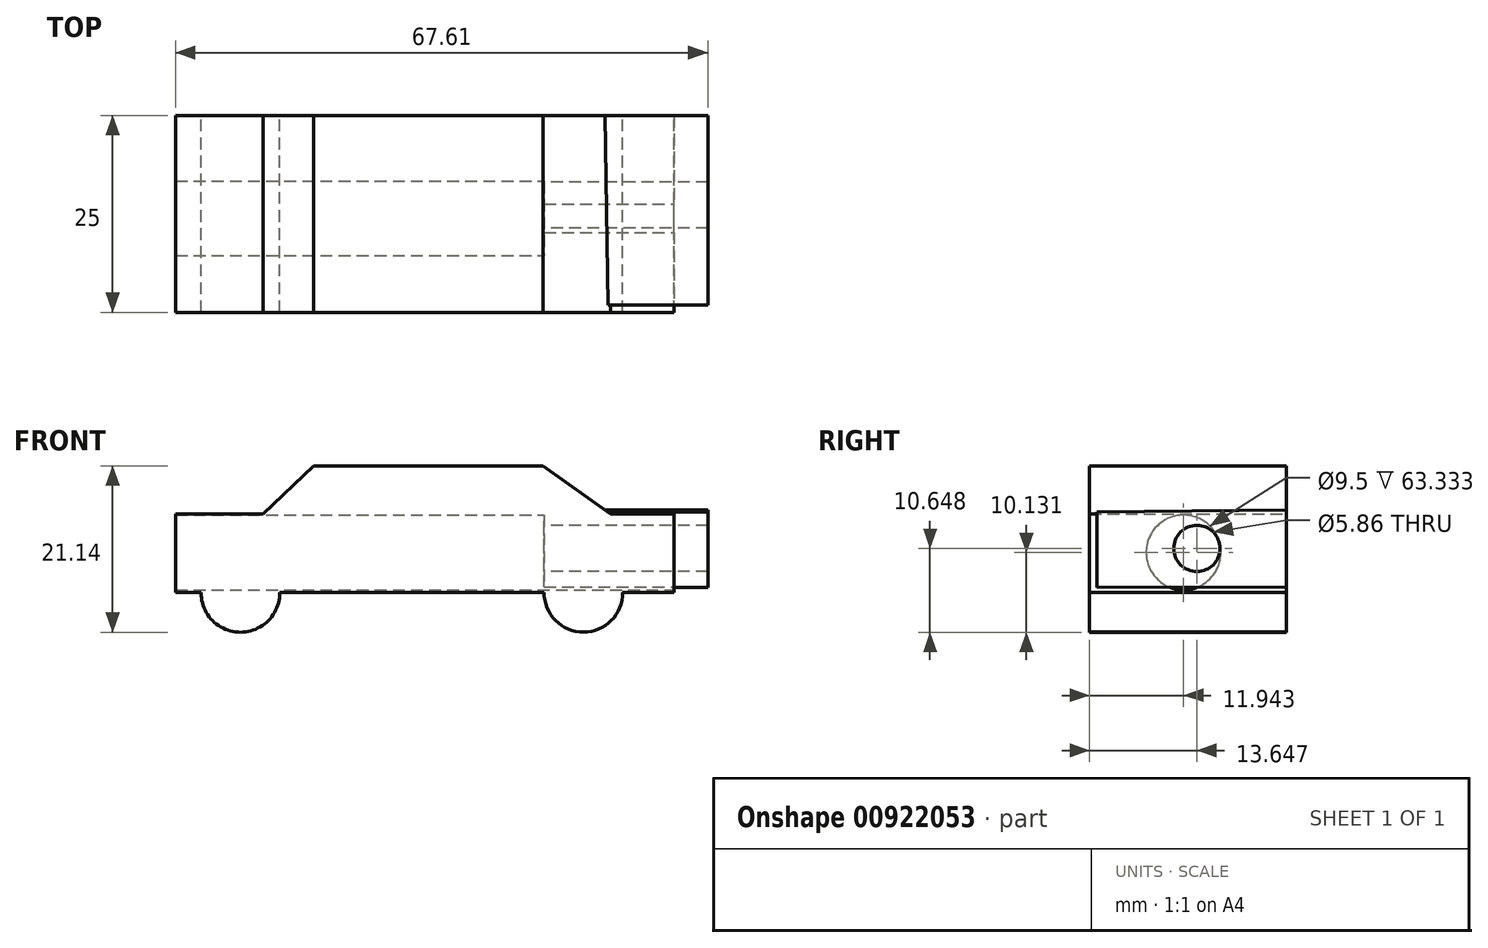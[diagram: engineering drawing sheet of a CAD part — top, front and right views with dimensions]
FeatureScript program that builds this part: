
annotation { "Feature Type Name" : "Feature", "Feature Type Description" : "" }
export const myFeature = defineFeature(function(context is Context, id is Id, definition is map)
    precondition{}
    {
        {
            var Q0;
            Q0=qCreatedBy(makeId("Front.planeOp"),FACE);
            var sketch = newSketch(context, id + "F0", { "sketchPlane" : qUnion([Q0])});
            skLineSegment(sketch, "E0", {"start": v(16.23, 9.06) * mm, "end": v(15.52, 9.06) * mm});
            skLineSegment(sketch, "E1", {"start": v(-46.8, 12.92) * mm, "end": v(-46.8, 22.92) * mm});
            skLineSegment(sketch, "E2", {"start": v(-46.8, 22.92) * mm, "end": v(-35.7, 22.92) * mm});
            skLineSegment(sketch, "E3", {"start": v(-35.7, 22.92) * mm, "end": v(-29.3, 29.03) * mm});
            skLineSegment(sketch, "E4", {"start": v(-29.3, 29.03) * mm, "end": v(0, 29.03) * mm});
            skLineSegment(sketch, "E5", {"start": v(-0.14, 29.03) * mm, "end": v(8.47, 22.92) * mm});
            skLineSegment(sketch, "E6", {"start": v(8.47, 22.92) * mm, "end": v(16.53, 22.92) * mm});
            skLineSegment(sketch, "E7", {"start": v(16.53, 22.92) * mm, "end": v(16.53, 12.92) * mm});
            skLineSegment(sketch, "E8", {"start": v(16.53, 12.92) * mm, "end": v(8.47, 12.92) * mm});
            skPoint(sketch, "E9", {"position": v(0, 12.92) * mm});
            skLineSegment(sketch, "E10.trimOffspring", {"start": v(0, 12.92) * mm, "end": v(-29.3, 12.92) * mm});
            skPoint(sketch, "E11.centerSnap0", {"position": v(-32.5, 25.97) * mm});
            skPoint(sketch, "E12.center.orphan", {"position": v(5, 12.92) * mm});
            skCircle(sketch, "E13", {"center": v(5, 12.92) * mm, "radius": 5 * mm});
            skCircle(sketch, "E14", {"center": v(-38.57, 12.89) * mm, "radius": 5 * mm});
            skLineSegment(sketch, "E15", {"start": v(-46.8, 12.92) * mm, "end": v(-43.57, 12.92) * mm});
            skLineSegment(sketch, "E16", {"start": v(-29.3, 12.92) * mm, "end": v(-33.57, 12.92) * mm});
            skSolve(sketch);
        }
        {
            var Q0;
            Q0 = qSketchRegion(id + "F0", true);
            extrude(context, id + "F1", {"entities" : qUnion([Q0]), "depth" : 25 * mm, "offsetDistance" : 25 * mm});
        }
        {
            var Q0;
            Q0=qCreatedBy(makeId("Right.planeOp"),FACE);
            var sketch = newSketch(context, id + "F2", { "sketchPlane" : qUnion([Q0])});
            skCircle(sketch, "E17", {"center": v(-13.06, 18.02) * mm, "radius": 4.75 * mm});
            skSolve(sketch);
        }
        {
            var Q0;
            Q0 = qSketchRegion(id + "F2", true);
            extrude(context, id + "F3", {"entities" : qUnion([Q0]), "operationType" : NewBodyOperationType.REMOVE, "endBound" : BoundingType.SYMMETRIC, "oppositeDirection" : true, "depth" : 102.4 * mm, "offsetDistance" : 25 * mm});
        }
        {
            var Q0;
            Q0=qCreatedBy(makeId("Right.planeOp"),FACE);
            var sketch = newSketch(context, id + "F4", { "sketchPlane" : qUnion([Q0])});
            skPoint(sketch, "E18.start.orphan", {"position": v(0, 22.69) * mm});
            skPoint(sketch, "E19.end.orphan", {"position": v(0, 23.41) * mm});
            skLineSegment(sketch, "E20", {"start": v(-24.08, 23.17) * mm, "end": v(-24.08, 13.6) * mm});
            skLineSegment(sketch, "E21", {"start": v(0, 13.65) * mm, "end": v(0, 23.41) * mm});
            skLineSegment(sketch, "E22", {"start": v(-24.08, 23.17) * mm, "end": v(0, 23.41) * mm});
            skLineSegment(sketch, "E23", {"start": v(-24.08, 13.6) * mm, "end": v(0, 13.65) * mm});
            skLineSegment(sketch, "E24", {"start": v(0, 13.65) * mm, "end": v(-21.91, 13.6) * mm});
            skSolve(sketch);
        }
        {
            var Q0;
            Q0 = qSketchRegion(id + "F4", true);
            extrude(context, id + "F5", {"entities" : qUnion([Q0]), "operationType" : NewBodyOperationType.ADD, "depth" : 20.8 * mm, "offsetDistance" : 25 * mm});
        }
        {
            var Q0;
            Q0=qCreatedBy(makeId("Right.planeOp"),FACE);
            var sketch = newSketch(context, id + "F6", { "sketchPlane" : qUnion([Q0])});
            skCircle(sketch, "E25", {"center": v(-11.35, 18.54) * mm, "radius": 2.93 * mm});
            skSolve(sketch);
        }
        {
            var Q0;
            Q0 = qSketchRegion(id + "F6", true);
            extrude(context, id + "F7", {"entities" : qUnion([Q0]), "operationType" : NewBodyOperationType.REMOVE, "depth" : 45.7 * mm, "offsetDistance" : 25 * mm});
        }
    });
